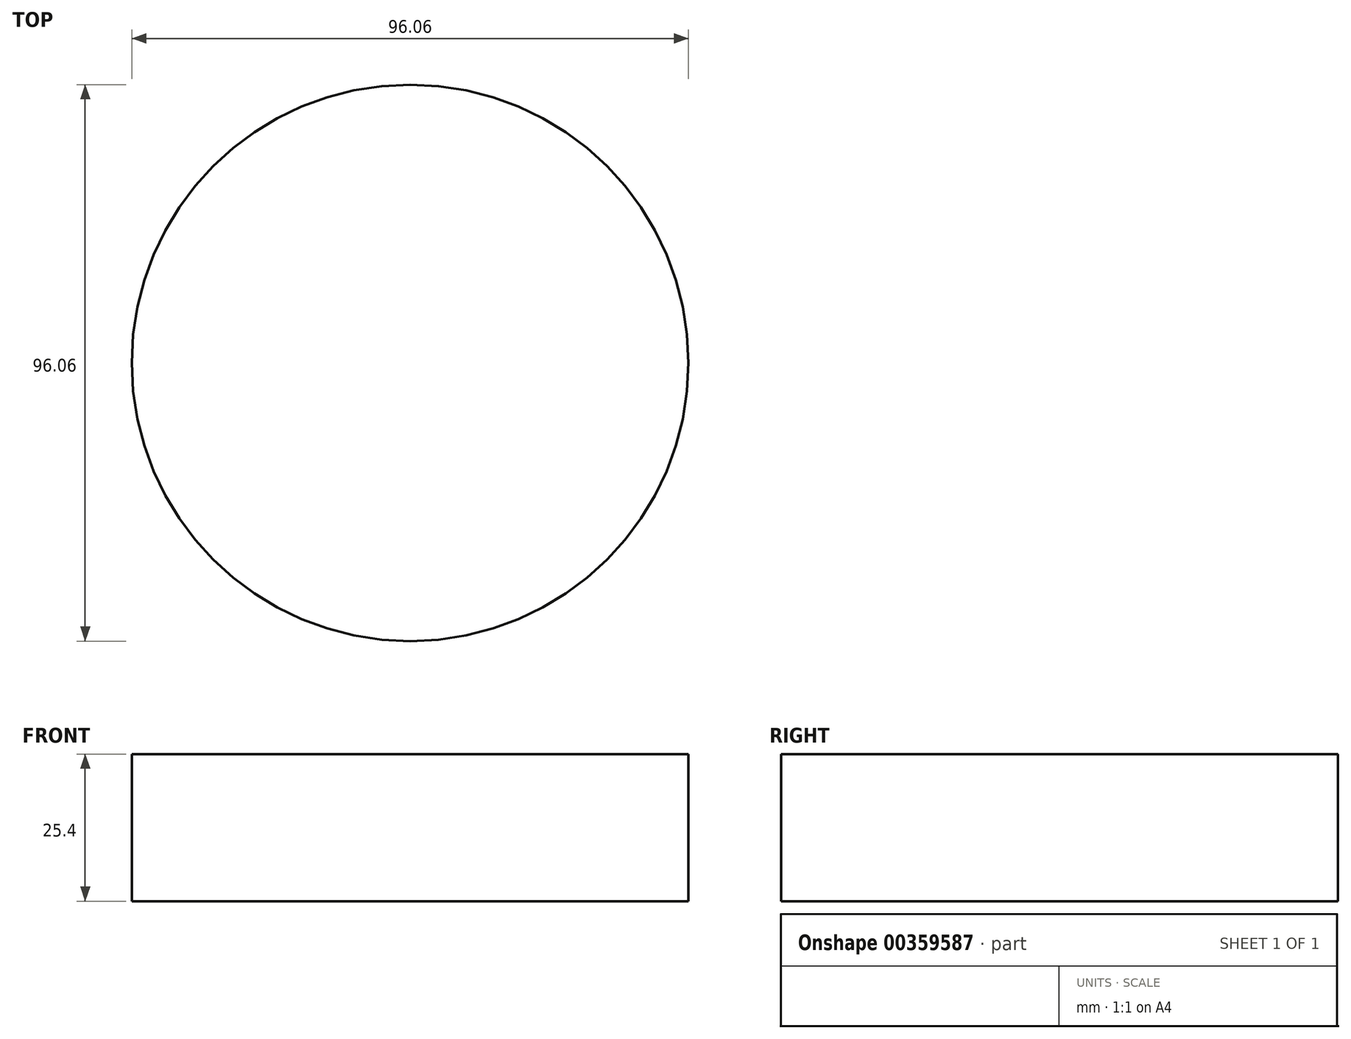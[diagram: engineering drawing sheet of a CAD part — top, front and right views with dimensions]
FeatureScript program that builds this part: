
annotation { "Feature Type Name" : "Feature", "Feature Type Description" : "" }
export const myFeature = defineFeature(function(context is Context, id is Id, definition is map)
    precondition{}
    {
        {
            var Q0;
            Q0=qCreatedBy(makeId("Top.planeOp"),FACE);
            var sketch = newSketch(context, id + "F0", { "sketchPlane" : qUnion([Q0])});
            skCircle(sketch, "E0", {"center": v(0, 0) * mm, "radius": 48.03 * mm});
            skSolve(sketch);
        }
        {
            var Q0;
            Q0=makeQuery(id+"F0.imprint","IMPRINT",FACE,{"disambiguationData":[TD([[makeQuery(id+"F0.imprint","IMPRINT",EDGE,{"derivedFrom":sQuery(id+"F0.wireOp",EDGE,"E0")}),1.0]])]});
            extrude(context, id + "F1", {"entities" : qUnion([Q0]), "depth" : 25.4 * mm});
        }
    });
